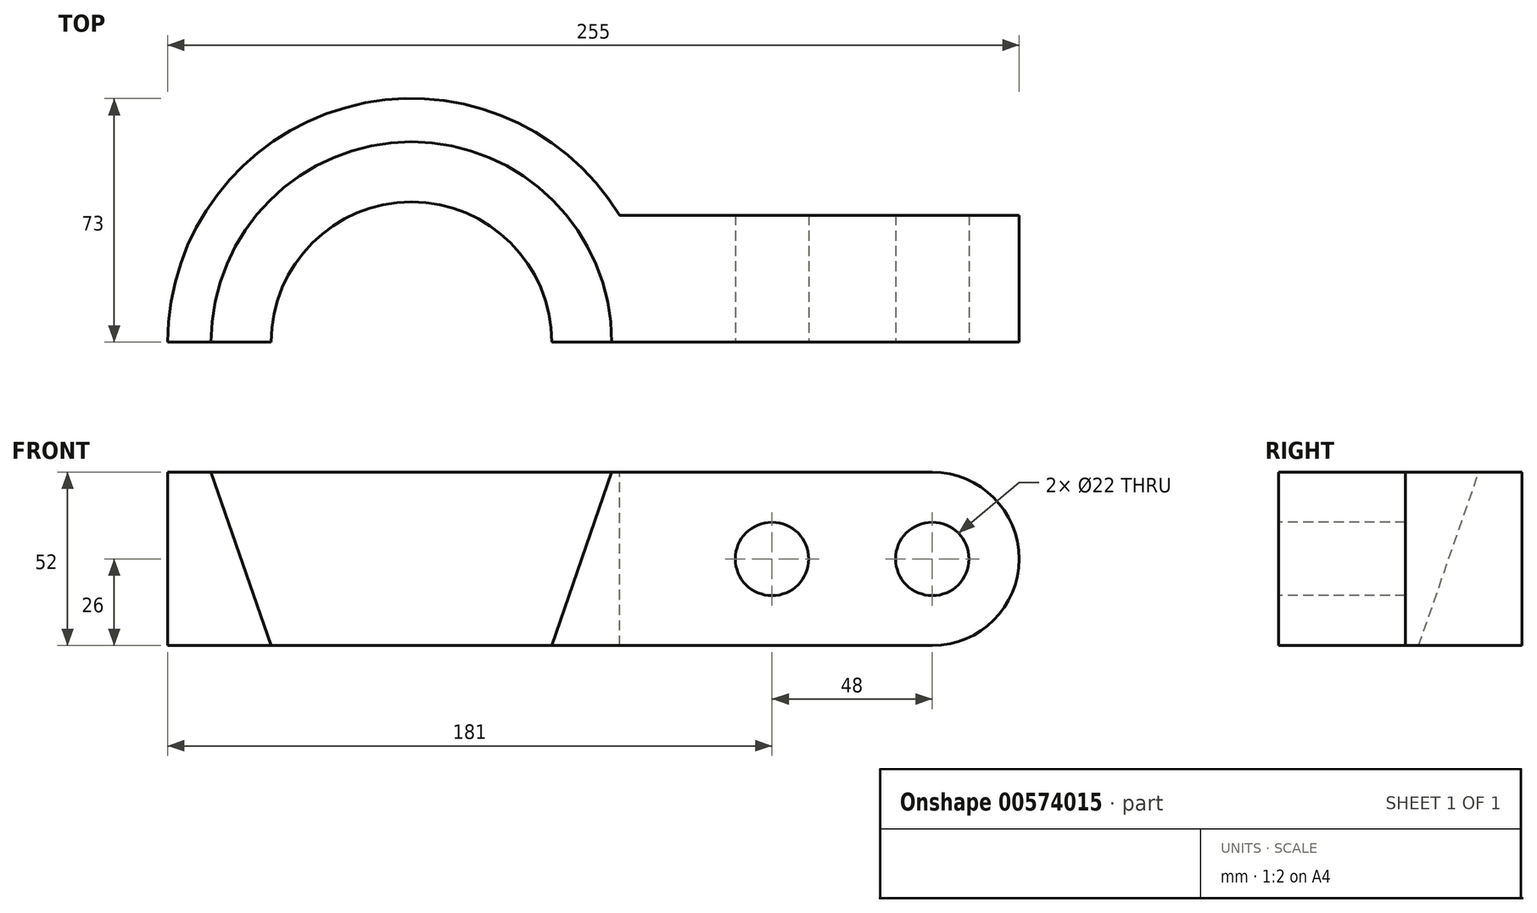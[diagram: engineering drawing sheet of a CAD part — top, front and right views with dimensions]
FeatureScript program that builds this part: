
annotation { "Feature Type Name" : "Feature", "Feature Type Description" : "" }
export const myFeature = defineFeature(function(context is Context, id is Id, definition is map)
    precondition{}
    {
        {
            var Q0;
            Q0=qCreatedBy(makeId("Front.planeOp"),FACE);
            var sketch = newSketch(context, id + "F0", { "sketchPlane" : qUnion([Q0])});
            skLineSegment(sketch, "E0", {"start": v(-73, 52) * mm, "end": v(-73, 0) * mm});
            skLineSegment(sketch, "E1", {"start": v(-73, 0) * mm, "end": v(-42, 0) * mm});
            skLineSegment(sketch, "E2", {"start": v(-42, 0) * mm, "end": v(-60, 52) * mm});
            skLineSegment(sketch, "E3", {"start": v(-60, 52) * mm, "end": v(-73, 52) * mm});
            skLineSegment(sketch, "E4", {"start": v(0, 74.67) * mm, "end": v(0, 0) * mm, "construction": true});
            skSolve(sketch);
        }
        {
            var Q0;
            Q0=makeQuery(id+"F0.imprint","IMPRINT",FACE,{"disambiguationData":[TD([[makeQuery(id+"F0.imprint","IMPRINT",EDGE,{"derivedFrom":sQuery(id+"F0.wireOp",EDGE,"E0")}),1.0]])]});
            var Q1;
            Q1=sQuery(id+"F0.wireOp",EDGE,"E4");
            revolve(context, id + "F1", {"entities" : qUnion([Q0]), "axis" : qUnion([Q1]), "revolveType" : RevolveType.ONE_DIRECTION, "angle" : 180 * degree});
        }
        {
            var Q0;
            Q0=qCreatedBy(makeId("Front.planeOp"),FACE);
            var sketch = newSketch(context, id + "F2", { "sketchPlane" : qUnion([Q0])});
            skLineSegment(sketch, "E5", {"start": v(156, 52) * mm, "end": v(60, 52) * mm});
            skLineSegment(sketch, "E6", {"start": v(60, 52) * mm, "end": v(42, 0) * mm});
            skLineSegment(sketch, "E7", {"start": v(42, 0) * mm, "end": v(156, 0) * mm});
            skArc(sketch, "E8", {"start": v(156, 0) * mm, "mid": v(182, 26) * mm, "end": v(156, 52) * mm});
            skSolve(sketch);
        }
        {
            var Q0;
            Q0=makeQuery(id+"F2.imprint","IMPRINT",FACE,{"disambiguationData":[TD([[makeQuery(id+"F2.imprint","IMPRINT",EDGE,{"derivedFrom":sQuery(id+"F2.wireOp",EDGE,"E5")}),1.0]])]});
            extrude(context, id + "F3", {"entities" : qUnion([Q0]), "operationType" : NewBodyOperationType.ADD, "oppositeDirection" : true, "depth" : 38 * mm, "offsetDistance" : 25 * mm});
        }
        {
            var Q0;
            Q0=makeQuery(id+"F3.boolean.opBoolean","MERGE",FACE,{"derivedFrom":[makeQuery(id+"F1.opRevolve","CAP_FACE",FACE,{"disambiguationData":[OSD([sQuery(id+"F0.wireOp",EDGE,"E0"),sQuery(id+"F0.wireOp",EDGE,"E1"),sQuery(id+"F0.wireOp",EDGE,"E2"),sQuery(id+"F0.wireOp",EDGE,"E3")])],"isStart":false}),makeQuery(id+"F3.opExtrude","CAP_FACE",FACE,{"disambiguationData":[OSD([sQuery(id+"F2.wireOp",EDGE,"E5"),sQuery(id+"F2.wireOp",EDGE,"E6"),sQuery(id+"F2.wireOp",EDGE,"E7"),sQuery(id+"F2.wireOp",EDGE,"E8")])],"isStart":true})]});
            var sketch = newSketch(context, id + "F4", { "sketchPlane" : qUnion([Q0])});
            skCircle(sketch, "E9", {"center": v(156, 26) * mm, "radius": 11 * mm});
            skCircle(sketch, "E10", {"center": v(108, 26) * mm, "radius": 11 * mm});
            skSolve(sketch);
        }
        {
            var Q0;
            Q0=makeQuery(id+"F4.imprint","IMPRINT",FACE,{"disambiguationData":[TD([[makeQuery(id+"F4.imprint","IMPRINT",EDGE,{"derivedFrom":sQuery(id+"F4.wireOp",EDGE,"E9")}),1.0]])]});
            var Q1;
            Q1=makeQuery(id+"F4.imprint","IMPRINT",FACE,{"disambiguationData":[TD([[makeQuery(id+"F4.imprint","IMPRINT",EDGE,{"derivedFrom":sQuery(id+"F4.wireOp",EDGE,"E10")}),1.0]])]});
            extrude(context, id + "F5", {"entities" : qUnion([Q0, Q1]), "operationType" : NewBodyOperationType.REMOVE, "oppositeDirection" : true, "depth" : 117 * mm, "offsetDistance" : 25 * mm});
        }
    });
